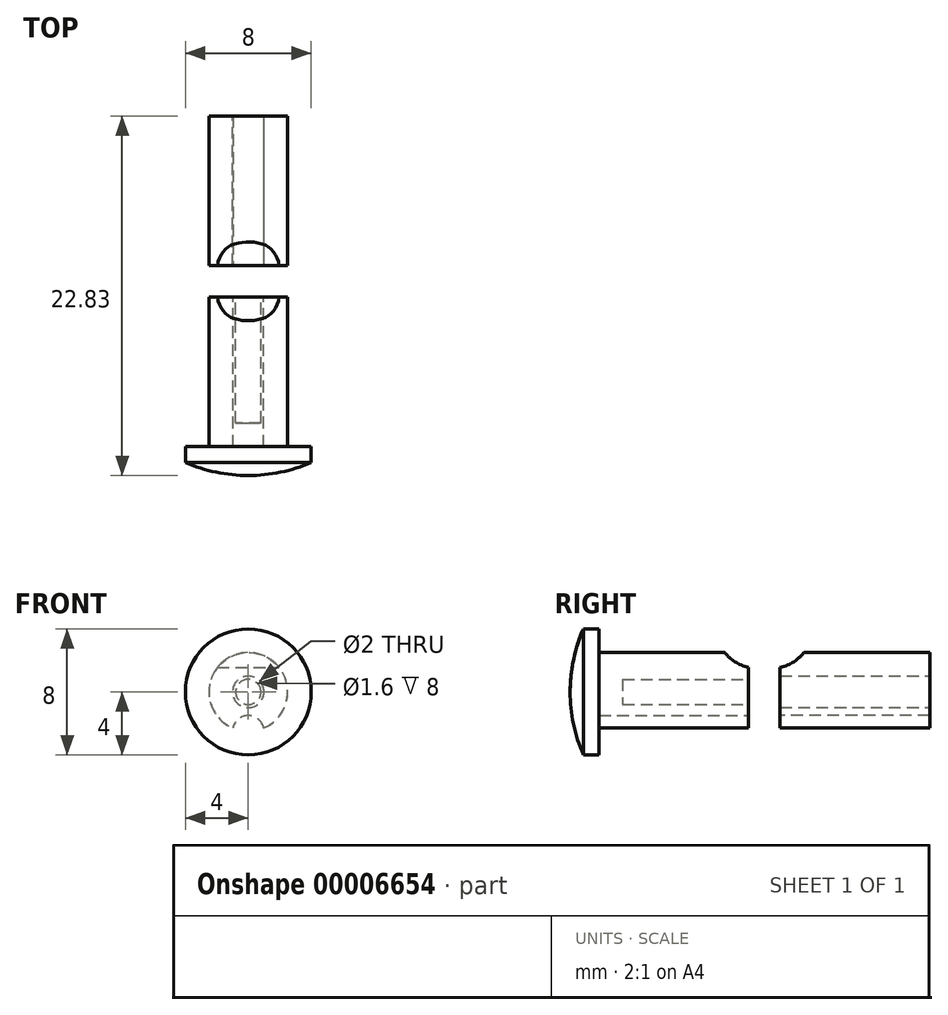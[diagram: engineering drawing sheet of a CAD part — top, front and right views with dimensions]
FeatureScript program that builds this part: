
annotation { "Feature Type Name" : "Feature", "Feature Type Description" : "" }
export const myFeature = defineFeature(function(context is Context, id is Id, definition is map)
    precondition{}
    {
        {
            var Q0;
            Q0=qCreatedBy(makeId("Front.planeOp"),FACE);
            var sketch = newSketch(context, id + "F0", { "sketchPlane" : qUnion([Q0])});
            skCircle(sketch, "E0", {"center": v(0, 0) * mm, "radius": 2.5 * mm});
            skSolve(sketch);
        }
        {
            var Q0;
            Q0 = qSketchRegion(id + "F0", true);
            extrude(context, id + "F1", {"entities" : qUnion([Q0]), "oppositeDirection" : true, "depth" : 9.5 * mm});
        }
        {
            var Q0;
            Q0=qCreatedBy(makeId("Right.planeOp"),FACE);
            var sketch = newSketch(context, id + "F2", { "sketchPlane" : qUnion([Q0])});
            skCircle(sketch, "E1", {"center": v(10, 4) * mm, "radius": 2.5 * mm});
            skLineSegment(sketch, "E2.0", {"start": v(9.5, -2.5) * mm, "end": v(9.5, 2.5) * mm, "construction": true});
            skPoint(sketch, "E3", {"position": v(10, 1.5) * mm});
            skSolve(sketch);
        }
        {
            var Q0;
            Q0 = qSketchRegion(id + "F2", true);
            extrude(context, id + "F3", {"entities" : qUnion([Q0]), "operationType" : NewBodyOperationType.REMOVE, "endBound" : BoundingType.SYMMETRIC, "oppositeDirection" : true, "depth" : 10 * mm});
        }
        {
            var Q0;
            Q0=makeQuery(id+"F1.opExtrude","CAP_FACE",FACE,{"disambiguationData":[OSD([sQuery(id+"F0.wireOp",EDGE,"E0")])],"isStart":false});
            var sketch = newSketch(context, id + "F4", { "sketchPlane" : qUnion([Q0])});
            skArc(sketch, "E4.0", {"start": v(-1.96, 1.55) * mm, "mid": v(0, 2.5) * mm, "end": v(1.96, 1.55) * mm, "construction": true});
            skCircle(sketch, "E5", {"center": v(0, -2.5) * mm, "radius": 1 * mm});
            skSolve(sketch);
        }
        {
            var Q0;
            Q0 = qSketchRegion(id + "F4", true);
            extrude(context, id + "F5", {"entities" : qUnion([Q0]), "operationType" : NewBodyOperationType.REMOVE, "oppositeDirection" : true, "depth" : 25 * mm});
        }
        {
            var Q0;
            Q0=makeQuery(id+"F1.opExtrude","CAP_FACE",FACE,{"disambiguationData":[OSD([sQuery(id+"F0.wireOp",EDGE,"E0")])],"isStart":false});
            cPlane(context, id + "F6", {"entities" : qUnion([Q0]), "cplaneType" : CPlaneType.OFFSET, "offset" : 1 * mm, "width" : 150 * mm, "height" : 150 * mm});
        }
        {
            var Q0;
            Q0=makeQuery(id+"F1.opExtrude","SWEPT_BODY",BODY,{"disambiguationData":[OSD([sQuery(id+"F0.wireOp",EDGE,"E0")])]});
            var Q1;
            Q1=qCreatedBy(id+"F6.planeOp",FACE);
            mirror(context, id + "F7", {"entities" : qUnion([Q0]), "mirrorPlane" : qUnion([Q1])});
        }
        {
            var Q0;
            Q0=makeQuery(id+"F1.opExtrude","CAP_FACE",FACE,{"disambiguationData":[OSD([sQuery(id+"F0.wireOp",EDGE,"E0")])],"isStart":true});
            var sketch = newSketch(context, id + "F8", { "sketchPlane" : qUnion([Q0])});
            skCircle(sketch, "E6", {"center": v(0, 0) * mm, "radius": 4 * mm});
            skSolve(sketch);
        }
        {
            var Q0;
            Q0 = qSketchRegion(id + "F8", true);
            extrude(context, id + "F9", {"entities" : qUnion([Q0]), "operationType" : NewBodyOperationType.ADD, "depth" : 1 * mm});
        }
        {
            var Q0;
            Q0=qCreatedBy(makeId("Right.planeOp"),FACE);
            var sketch = newSketch(context, id + "F10", { "sketchPlane" : qUnion([Q0])});
            skLineSegment(sketch, "E7.0", {"start": v(-1, -4) * mm, "end": v(-1, 4) * mm});
            skLineSegment(sketch, "E8", {"start": v(-1, 0) * mm, "end": v(-3.8, 0) * mm});
            skArc(sketch, "E9", {"start": v(-1, 4) * mm, "mid": v(-1.62, 2.04) * mm, "end": v(-1.83, 0) * mm});
            skSolve(sketch);
        }
        {
            var Q0;
            Q0 = qSketchRegion(id + "F10", true);
            var Q1;
            Q1=sQuery(id+"F10.wireOp",EDGE,"E8");
            revolve(context, id + "F11", {"operationType" : NewBodyOperationType.ADD, "entities" : qUnion([Q0]), "axis" : qUnion([Q1]), "revolveType" : RevolveType.FULL});
        }
        {
            var Q0;
            Q0=makeQuery(id+"F1.opExtrude","CAP_FACE",FACE,{"disambiguationData":[OSD([sQuery(id+"F0.wireOp",EDGE,"E0")])],"isStart":false});
            var sketch = newSketch(context, id + "F12", { "sketchPlane" : qUnion([Q0])});
            skArc(sketch, "E10.0", {"start": v(1.96, 1.55) * mm, "mid": v(-1.96, -1.55) * mm, "end": v(1.96, 1.55) * mm, "construction": true});
            skCircle(sketch, "E11", {"center": v(0, 0) * mm, "radius": 0.8 * mm});
            skSolve(sketch);
        }
        {
            var Q0;
            Q0 = qSketchRegion(id + "F12", true);
            extrude(context, id + "F13", {"entities" : qUnion([Q0]), "operationType" : NewBodyOperationType.REMOVE, "oppositeDirection" : true, "depth" : 8 * mm});
        }
        {
            var Q0;
            Q0=makeQuery(id+"F7.opPattern","COPY",FACE,{"derivedFrom":makeQuery(id+"F1.opExtrude","CAP_FACE",FACE,{"disambiguationData":[OSD([sQuery(id+"F0.wireOp",EDGE,"E0")])],"isStart":true}),"instanceName":"1"});
            var sketch = newSketch(context, id + "F14", { "sketchPlane" : qUnion([Q0])});
            skCircle(sketch, "E12.0", {"center": v(0, 0) * mm, "radius": 2.5 * mm, "construction": true});
            skCircle(sketch, "E13", {"center": v(0, 0) * mm, "radius": 1 * mm});
            skSolve(sketch);
        }
        {
            var Q0;
            Q0 = qSketchRegion(id + "F14", true);
            extrude(context, id + "F15", {"entities" : qUnion([Q0]), "operationType" : NewBodyOperationType.REMOVE, "oppositeDirection" : true, "depth" : 10.4 * mm});
        }
    });
